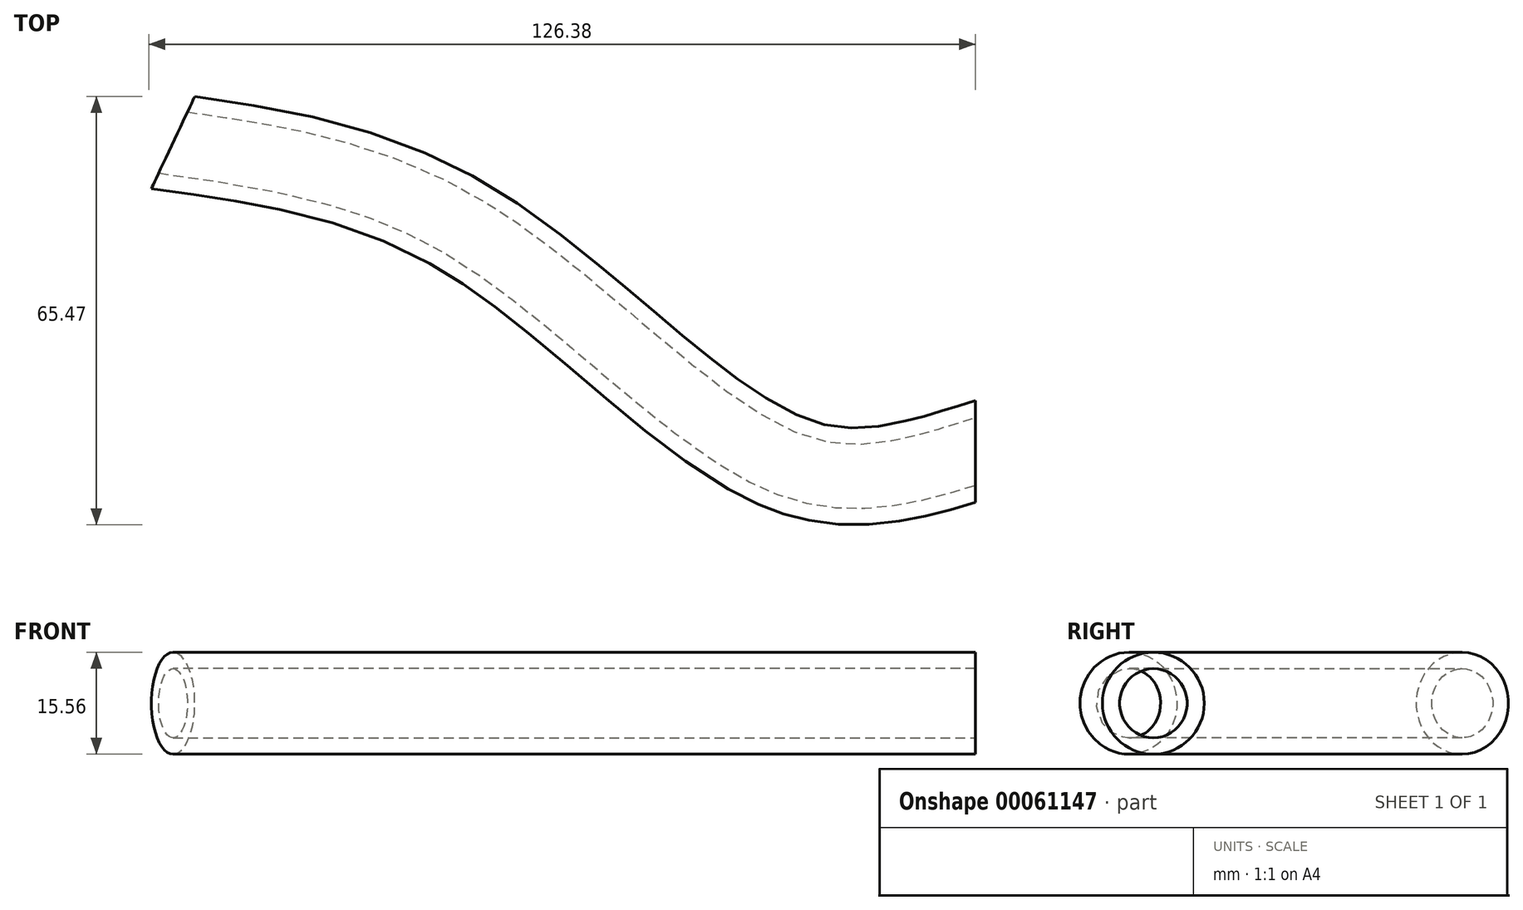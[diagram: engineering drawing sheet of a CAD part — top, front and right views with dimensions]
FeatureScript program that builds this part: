
annotation { "Feature Type Name" : "Feature", "Feature Type Description" : "" }
export const myFeature = defineFeature(function(context is Context, id is Id, definition is map)
    precondition{}
    {
        {
            var Q0;
            Q0=qCreatedBy(makeId("Top.planeOp"),FACE);
            var sketch = newSketch(context, id + "F0", { "sketchPlane" : qUnion([Q0])});
            skFitSpline(sketch, "E0", {"points": [v(-52.68, 25.64) * mm, v(-7, 11.96) * mm, v(41.5, -23.47) * mm, v(70.08, -21.6) * mm], "startDerivative": vector(132.82, -18.92) * mm, "endDerivative": vector(103.24, 31.83) * mm});
            skSolve(sketch);
        }
        {
            var Q0;
            Q0=sQuery(id+"F0.wireOp",VERTEX,"E0.3.internal");
            var Q1;
            Q1=qCreatedBy(makeId("Right.planeOp"),FACE);
            cPlane(context, id + "F1", {"entities" : qUnion([Q0, Q1]), "cplaneType" : CPlaneType.PLANE_POINT, "offset" : 150 * mm, "width" : 150 * mm, "height" : 150 * mm});
        }
        {
            var Q0;
            Q0=qCreatedBy(id+"F1.planeOp",FACE);
            var sketch = newSketch(context, id + "F2", { "sketchPlane" : qUnion([Q0])});
            skCircle(sketch, "E1", {"center": v(-21.35, 0) * mm, "radius": 7.78 * mm});
            skSolve(sketch);
        }
        {
            var Q0;
            Q0=makeQuery(id+"F2.imprint","IMPRINT",FACE,{"disambiguationData":[TD([[makeQuery(id+"F2.imprint","IMPRINT",EDGE,{"derivedFrom":sQuery(id+"F2.wireOp",EDGE,"E1")}),1.0]])]});
            var Q1;
            Q1=sQuery(id+"F0.wireOp",EDGE,"E0");
            sweep(context, id + "F3", {"profiles" : qUnion([Q0]), "path" : qUnion([Q1])});
        }
        {
            var Q0;
            Q0=makeQuery(id+"F3.opSweep","CAP_FACE",FACE,{"disambiguationData":[OSD([sQuery(id+"F0.wireOp",VERTEX,"E0.end"),sQuery(id+"F2.wireOp",EDGE,"E1")])],"isStart":true});
            var Q1;
            Q1=makeQuery(id+"F3.opSweep","CAP_FACE",FACE,{"disambiguationData":[OSD([sQuery(id+"F0.wireOp",VERTEX,"E0.start"),sQuery(id+"F2.wireOp",EDGE,"E1")])],"isStart":false});
            shell(context, id + "F4", {"entities" : qUnion([Q0, Q1]), "thickness" : 2.5 * mm});
        }
    });
